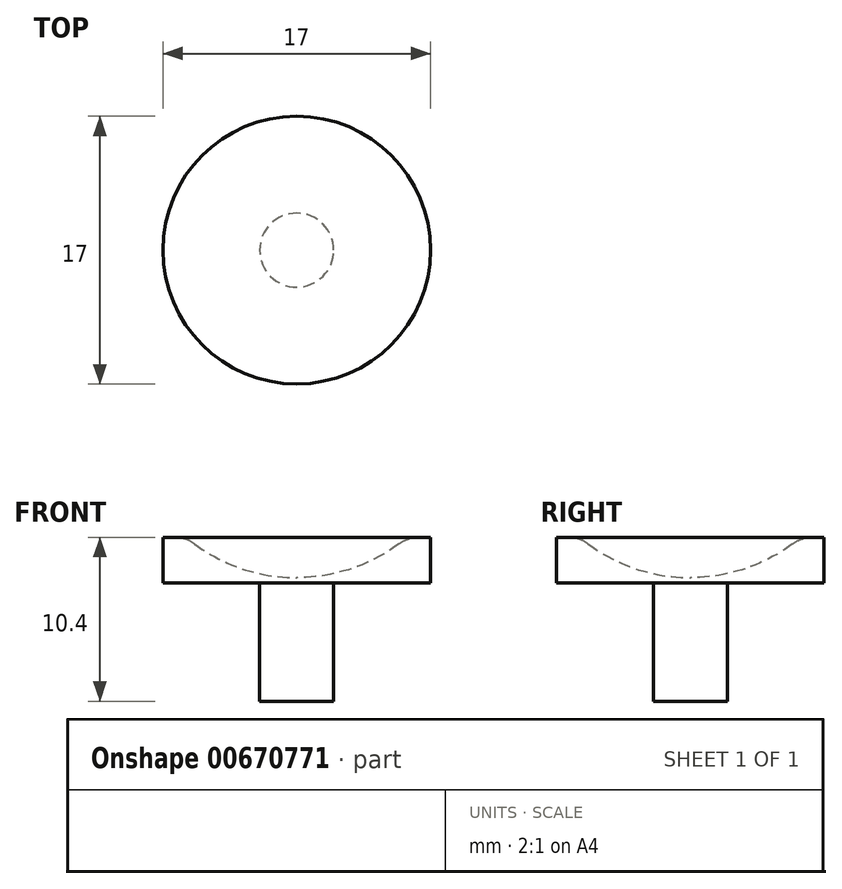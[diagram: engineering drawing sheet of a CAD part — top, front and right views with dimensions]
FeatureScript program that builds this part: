
annotation { "Feature Type Name" : "Feature", "Feature Type Description" : "" }
export const myFeature = defineFeature(function(context is Context, id is Id, definition is map)
    precondition{}
    {
        {
            var Q0;
            Q0=qCreatedBy(makeId("Front.planeOp"),FACE);
            var sketch = newSketch(context, id + "F0", { "sketchPlane" : qUnion([Q0])});
            skLineSegment(sketch, "E0", {"start": v(0, 0) * mm, "end": v(0, 7.84) * mm, "construction": true});
            skLineSegment(sketch, "E1", {"start": v(0, 0) * mm, "end": v(-2.35, 0) * mm});
            skLineSegment(sketch, "E2", {"start": v(-2.35, 0) * mm, "end": v(-2.35, 7.5) * mm});
            skLineSegment(sketch, "E3", {"start": v(-2.35, 7.5) * mm, "end": v(-8.5, 7.5) * mm});
            skLineSegment(sketch, "E4", {"start": v(-8.5, 7.5) * mm, "end": v(-8.5, 10.4) * mm});
            skLineSegment(sketch, "E5", {"start": v(-8.5, 10.4) * mm, "end": v(-7, 10.4) * mm});
            skLineSegment(sketch, "E6", {"start": v(0, 7.84) * mm, "end": v(0, 0) * mm});
            skArc(sketch, "E7", {"start": v(-7, 10.4) * mm, "mid": v(-3.73, 8.5) * mm, "end": v(0, 7.84) * mm});
            skPoint(sketch, "E8.orphan", {"position": v(0, 10.4) * mm});
            skSolve(sketch);
        }
        {
            var Q0;
            Q0 = qSketchRegion(id + "F0", true);
            var Q1;
            Q1=sQuery(id+"F0.wireOp",EDGE,"E6");
            revolve(context, id + "F1", {"entities" : qUnion([Q0]), "axis" : qUnion([Q1]), "revolveType" : RevolveType.FULL});
        }
        {
            var Q0;
            Q0=makeQuery(id+"F1.opRevolve","SWEPT_EDGE",EDGE,{"disambiguationData":[OSD([sQuery(id+"F0.wireOp",EDGE,"E5"),sQuery(id+"F0.wireOp",EDGE,"E7")])]});
            fillet(context, id + "F2", {"entities" : qUnion([Q0]), "radius" : 2 * mm, "tangentPropagation" : true, "allowEdgeOverflow" : false});
        }
    });
